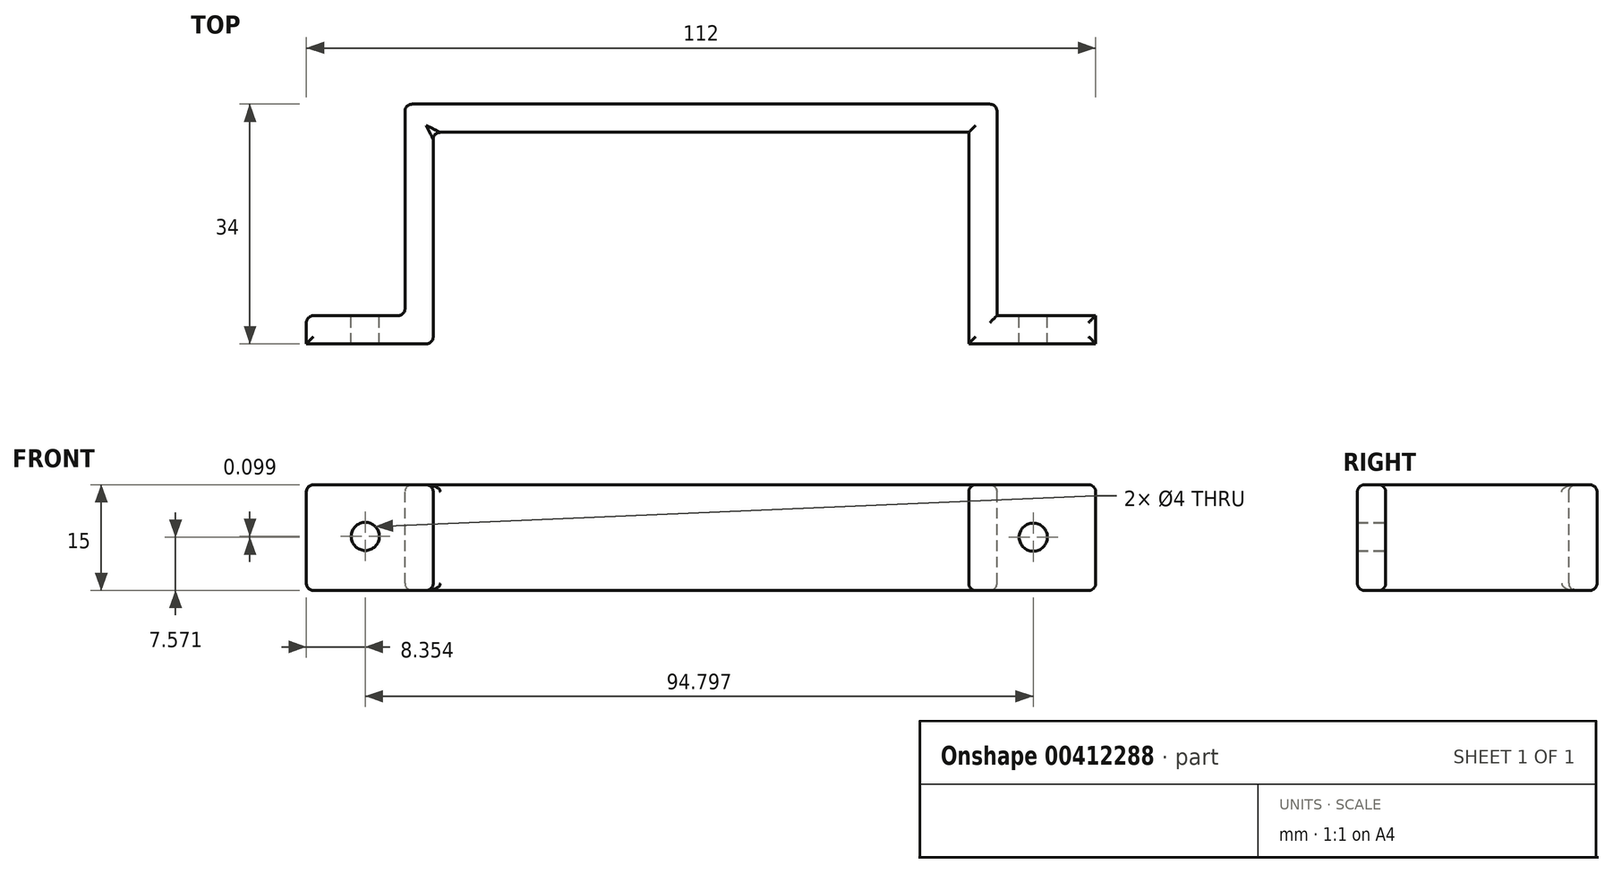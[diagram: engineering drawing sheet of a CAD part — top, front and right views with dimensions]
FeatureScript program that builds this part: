
annotation { "Feature Type Name" : "Feature", "Feature Type Description" : "" }
export const myFeature = defineFeature(function(context is Context, id is Id, definition is map)
    precondition{}
    {
        {
            var Q0;
            Q0=qCreatedBy(makeId("Top.planeOp"),FACE);
            var sketch = newSketch(context, id + "F0", { "sketchPlane" : qUnion([Q0])});
            skLineSegment(sketch, "E0", {"start": v(0, 0) * mm, "end": v(-42, 0) * mm});
            skLineSegment(sketch, "E1", {"start": v(-42, 0) * mm, "end": v(-42, -30) * mm});
            skLineSegment(sketch, "E2", {"start": v(-42, -30) * mm, "end": v(-56, -30) * mm});
            skLineSegment(sketch, "E3", {"start": v(0, -60) * mm, "end": v(0, -37.04) * mm, "construction": true});
            skPoint(sketch, "E4.MirrorCS.start.orphan", {"position": v(0, -60) * mm});
            skLineSegment(sketch, "E5.trimOffspring", {"start": v(0, 0) * mm, "end": v(0, 57.79) * mm, "construction": true});
            skPoint(sketch, "E6.MirrorCS.end.orphan", {"position": v(-42, -30) * mm});
            skPoint(sketch, "E6.MirrorCS.start.orphan", {"position": v(-42, -60) * mm});
            skLineSegment(sketch, "E7.0", {"start": v(-38, -34) * mm, "end": v(-56, -34) * mm});
            skLineSegment(sketch, "E7.1", {"start": v(-38, -4) * mm, "end": v(-38, -34) * mm});
            skLineSegment(sketch, "E7.5", {"start": v(0, -4) * mm, "end": v(-38, -4) * mm});
            skLineSegment(sketch, "E8", {"start": v(-56, -34) * mm, "end": v(-56, -30) * mm});
            skPoint(sketch, "E9.MirrorCS.end.orphan", {"position": v(42, 0) * mm});
            skLineSegment(sketch, "E10.MirrorCS", {"start": v(0, 0) * mm, "end": v(42, 0) * mm});
            skLineSegment(sketch, "E11.MirrorCS", {"start": v(0, -4) * mm, "end": v(38, -4) * mm});
            skLineSegment(sketch, "E12.MirrorCS", {"start": v(42, 0) * mm, "end": v(42, -30) * mm});
            skLineSegment(sketch, "E13.MirrorCS", {"start": v(38, -4) * mm, "end": v(38, -34) * mm});
            skLineSegment(sketch, "E14.MirrorCS", {"start": v(42, -30) * mm, "end": v(56, -30) * mm});
            skLineSegment(sketch, "E15.MirrorCS", {"start": v(38, -34) * mm, "end": v(56, -34) * mm});
            skLineSegment(sketch, "E16.MirrorCS", {"start": v(56, -34) * mm, "end": v(56, -30) * mm});
            skSolve(sketch);
        }
        {
            var Q0;
            Q0 = qSketchRegion(id + "F0", true);
            extrude(context, id + "F1", {"entities" : qUnion([Q0]), "oppositeDirection" : true, "depth" : 15 * mm});
        }
        {
            var Q0;
            Q0=makeQuery(id+"F1.opExtrude","SWEPT_FACE",FACE,{"disambiguationData":[OSD([sQuery(id+"F0.wireOp",EDGE,"E0"),sQuery(id+"F0.wireOp",EDGE,"E9.MirrorCS")])]});
            var Q1;
            Q1=makeQuery(id+"F1.opExtrude","SWEPT_FACE",FACE,{"disambiguationData":[OSD([sQuery(id+"F0.wireOp",EDGE,"4b06f142-9d04-46d7-ba52-2e396e7723cf0.MirrorCS")])]});
            var Q2;
            Q2=makeQuery(id+"F1.opExtrude","SWEPT_FACE",FACE,{"disambiguationData":[OSD([sQuery(id+"F0.wireOp",EDGE,"E2")])]});
            var Q3;
            Q3=makeQuery(id+"F1.opExtrude","CAP_FACE",FACE,{"disambiguationData":[OSD([sQuery(id+"F0.wireOp",EDGE,"E0"),sQuery(id+"F0.wireOp",EDGE,"E1"),sQuery(id+"F0.wireOp",EDGE,"E2"),sQuery(id+"F0.wireOp",EDGE,"E9.MirrorCS"),sQuery(id+"F0.wireOp",EDGE,"8f052d92-5b77-4bcf-8aa6-04eb32446d620.MirrorCS"),sQuery(id+"F0.wireOp",EDGE,"4b06f142-9d04-46d7-ba52-2e396e7723cf0.MirrorCS"),sQuery(id+"F0.wireOp",EDGE,"E7.0"),sQuery(id+"F0.wireOp",EDGE,"E7.1"),sQuery(id+"F0.wireOp",EDGE,"E7.2"),sQuery(id+"F0.wireOp",EDGE,"E7.3"),sQuery(id+"F0.wireOp",EDGE,"E7.4"),sQuery(id+"F0.wireOp",EDGE,"E7.5"),sQuery(id+"F0.wireOp",EDGE,"irrUF8Ry-Fhgf-WQi6-O0jY-DwySnD11VG29"),sQuery(id+"F0.wireOp",EDGE,"E8")])],"isStart":true});
            var Q4;
            Q4=makeQuery(id+"F1.opExtrude","CAP_FACE",FACE,{"disambiguationData":[OSD([sQuery(id+"F0.wireOp",EDGE,"E0"),sQuery(id+"F0.wireOp",EDGE,"E1"),sQuery(id+"F0.wireOp",EDGE,"E2"),sQuery(id+"F0.wireOp",EDGE,"E9.MirrorCS"),sQuery(id+"F0.wireOp",EDGE,"8f052d92-5b77-4bcf-8aa6-04eb32446d620.MirrorCS"),sQuery(id+"F0.wireOp",EDGE,"4b06f142-9d04-46d7-ba52-2e396e7723cf0.MirrorCS"),sQuery(id+"F0.wireOp",EDGE,"E7.0"),sQuery(id+"F0.wireOp",EDGE,"E7.1"),sQuery(id+"F0.wireOp",EDGE,"E7.2"),sQuery(id+"F0.wireOp",EDGE,"E7.3"),sQuery(id+"F0.wireOp",EDGE,"E7.4"),sQuery(id+"F0.wireOp",EDGE,"E7.5"),sQuery(id+"F0.wireOp",EDGE,"irrUF8Ry-Fhgf-WQi6-O0jY-DwySnD11VG29"),sQuery(id+"F0.wireOp",EDGE,"E8")])],"isStart":false});
            fillet(context, id + "F2", {"entities" : qUnion([Q0, Q1, Q2, Q3, Q4]), "radius" : 1 * mm, "tangentPropagation" : true, "allowEdgeOverflow" : false});
        }
        {
            var Q0;
            Q0=makeQuery(id+"F1.opExtrude","SWEPT_EDGE",EDGE,{"disambiguationData":[OSD([sQuery(id+"F0.wireOp",EDGE,"E7.0"),sQuery(id+"F0.wireOp",EDGE,"E7.1")])]});
            var Q1;
            Q1=makeQuery(id+"F1.opExtrude","SWEPT_FACE",FACE,{"disambiguationData":[OSD([sQuery(id+"F0.wireOp",EDGE,"E7.3")])]});
            var Q2;
            Q2=makeQuery(id+"F1.opExtrude","SWEPT_FACE",FACE,{"disambiguationData":[OSD([sQuery(id+"F0.wireOp",EDGE,"E7.1")])]});
            fillet(context, id + "F3", {"entities" : qUnion([Q0, Q1, Q2]), "radius" : 1 * mm, "tangentPropagation" : true, "allowEdgeOverflow" : false});
        }
        {
            var Q0;
            Q0=makeQuery(id+"F1.opExtrude","SWEPT_FACE",FACE,{"disambiguationData":[OSD([sQuery(id+"F0.wireOp",EDGE,"E14.MirrorCS")])]});
            var sketch = newSketch(context, id + "F4", { "sketchPlane" : qUnion([Q0])});
            skCircle(sketch, "E17", {"center": v(-47.15, -7.43) * mm, "radius": 2 * mm});
            skCircle(sketch, "E18", {"center": v(47.65, -7.33) * mm, "radius": 2 * mm});
            skSolve(sketch);
        }
        {
            var Q0;
            Q0 = qSketchRegion(id + "F4", true);
            extrude(context, id + "F5", {"entities" : qUnion([Q0]), "operationType" : NewBodyOperationType.REMOVE, "endBound" : BoundingType.THROUGH_ALL, "oppositeDirection" : true, "depth" : 25 * mm});
        }
    });
